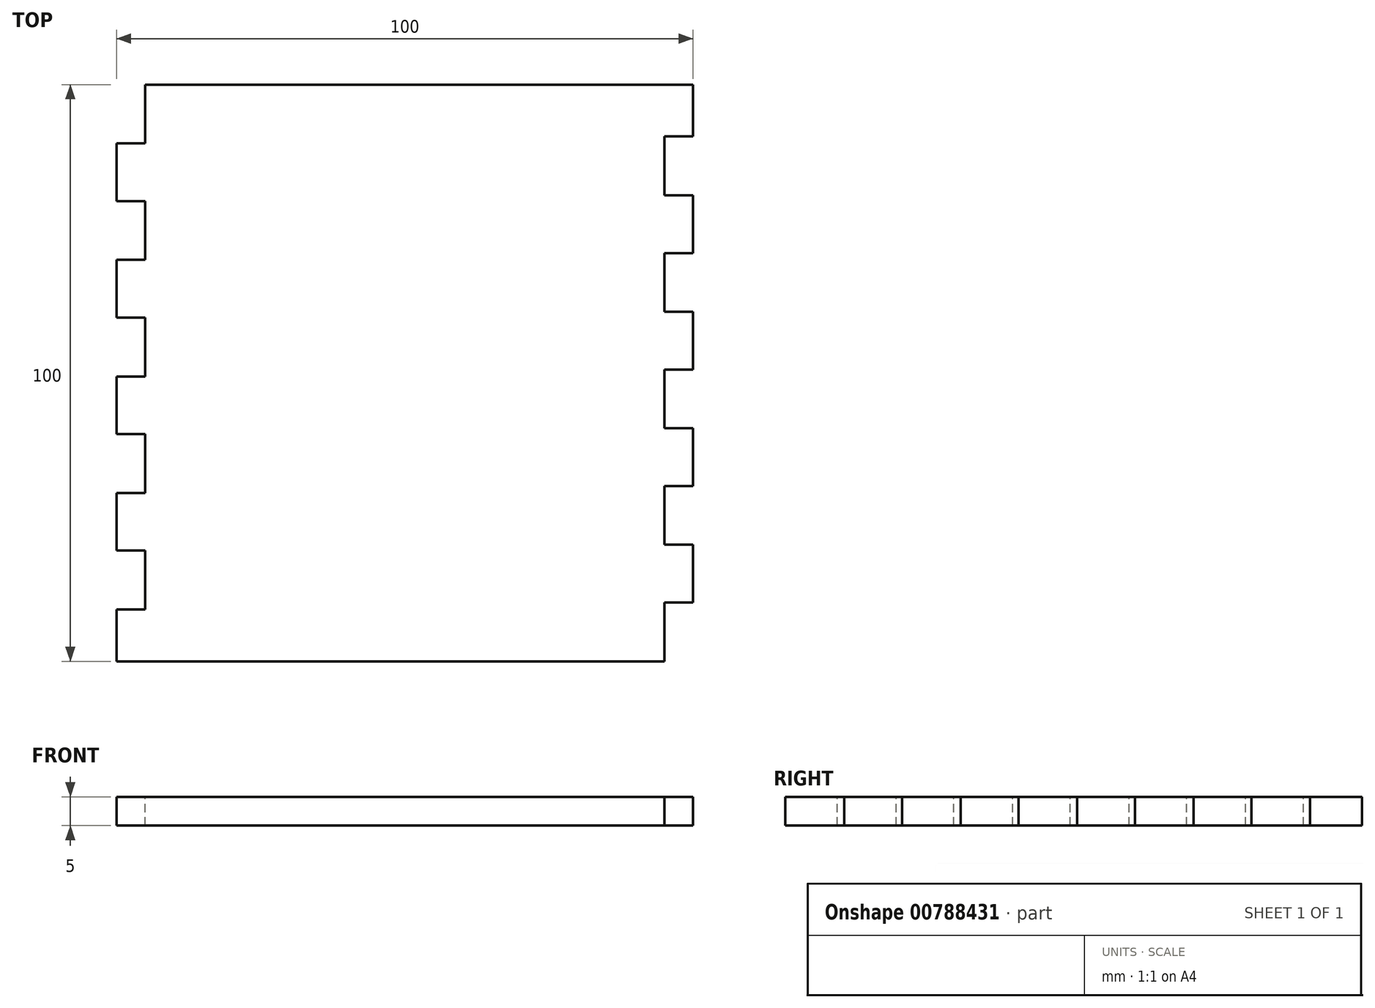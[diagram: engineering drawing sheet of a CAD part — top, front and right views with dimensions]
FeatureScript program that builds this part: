
annotation { "Feature Type Name" : "Feature", "Feature Type Description" : "" }
export const myFeature = defineFeature(function(context is Context, id is Id, definition is map)
    precondition{}
    {
        {
            var Q0;
            Q0=qCreatedBy(makeId("Top.planeOp"),FACE);
            var sketch = newSketch(context, id + "F0", { "sketchPlane" : qUnion([Q0])});
            skLineSegment(sketch, "E0.bottom", {"start": v(50, -50) * mm, "end": v(-50, -50) * mm});
            skLineSegment(sketch, "E0.top", {"start": v(50, 50) * mm, "end": v(-50, 50) * mm});
            skLineSegment(sketch, "E0.left", {"start": v(50, -50) * mm, "end": v(50, 50) * mm});
            skLineSegment(sketch, "E0.right", {"start": v(-50, -50) * mm, "end": v(-50, 50) * mm});
            skPoint(sketch, "E0.middle", {"position": v(0, 0) * mm});
            skSolve(sketch);
        }
        {
            var Q0;
            Q0 = qSketchRegion(id + "F0", true);
            extrude(context, id + "F1", {"entities" : qUnion([Q0]), "depth" : 5 * mm, "offsetDistance" : 25 * mm});
        }
        {
            var Q0;
            Q0=makeQuery(id+"F1.opExtrude","CAP_FACE",FACE,{"disambiguationData":[OSD([sQuery(id+"F0.wireOp",EDGE,"E0.bottom"),sQuery(id+"F0.wireOp",EDGE,"E0.top"),sQuery(id+"F0.wireOp",EDGE,"E0.left"),sQuery(id+"F0.wireOp",EDGE,"E0.right")])],"isStart":false});
            var sketch = newSketch(context, id + "F2", { "sketchPlane" : qUnion([Q0])});
            skLineSegment(sketch, "E1.bottom", {"start": v(-50, 50) * mm, "end": v(-45, 50) * mm});
            skLineSegment(sketch, "E1.top", {"start": v(-50, 39.8) * mm, "end": v(-45, 39.8) * mm});
            skLineSegment(sketch, "E1.left", {"start": v(-50, 50) * mm, "end": v(-50, 39.8) * mm});
            skLineSegment(sketch, "E1.right", {"start": v(-45, 50) * mm, "end": v(-45, 39.8) * mm});
            skLineSegment(sketch, "E2.bottom", {"start": v(-45, 29.8) * mm, "end": v(-50, 29.8) * mm});
            skLineSegment(sketch, "E2.top", {"start": v(-45, 19.6) * mm, "end": v(-50, 19.6) * mm});
            skLineSegment(sketch, "E2.left", {"start": v(-45, 29.8) * mm, "end": v(-45, 19.6) * mm});
            skLineSegment(sketch, "E2.right", {"start": v(-50, 29.8) * mm, "end": v(-50, 19.6) * mm});
            skLineSegment(sketch, "E3.bottom", {"start": v(-45, 9.6) * mm, "end": v(-50, 9.6) * mm});
            skLineSegment(sketch, "E3.top", {"start": v(-45, -0.6) * mm, "end": v(-50, -0.6) * mm});
            skLineSegment(sketch, "E3.left", {"start": v(-45, 9.6) * mm, "end": v(-45, -0.6) * mm});
            skLineSegment(sketch, "E3.right", {"start": v(-50, 9.6) * mm, "end": v(-50, -0.6) * mm});
            skLineSegment(sketch, "E4.bottom", {"start": v(-45, -10.6) * mm, "end": v(-50, -10.6) * mm});
            skLineSegment(sketch, "E4.top", {"start": v(-45, -20.8) * mm, "end": v(-50, -20.8) * mm});
            skLineSegment(sketch, "E4.left", {"start": v(-45, -10.6) * mm, "end": v(-45, -20.8) * mm});
            skLineSegment(sketch, "E4.right", {"start": v(-50, -10.6) * mm, "end": v(-50, -20.8) * mm});
            skLineSegment(sketch, "E5.bottom", {"start": v(-50, -30.8) * mm, "end": v(-45, -30.8) * mm});
            skLineSegment(sketch, "E5.top", {"start": v(-50, -41) * mm, "end": v(-45, -41) * mm});
            skLineSegment(sketch, "E5.left", {"start": v(-50, -30.8) * mm, "end": v(-50, -41) * mm});
            skLineSegment(sketch, "E5.right", {"start": v(-45, -30.8) * mm, "end": v(-45, -41) * mm});
            skSolve(sketch);
        }
        {
            var Q0;
            Q0 = qSketchRegion(id + "F2", true);
            extrude(context, id + "F3", {"entities" : qUnion([Q0]), "operationType" : NewBodyOperationType.REMOVE, "oppositeDirection" : true, "depth" : 5 * mm, "offsetDistance" : 25 * mm});
        }
        {
            var Q0;
            Q0=makeQuery(id+"F1.opExtrude","CAP_FACE",FACE,{"disambiguationData":[OSD([sQuery(id+"F0.wireOp",EDGE,"E0.bottom"),sQuery(id+"F0.wireOp",EDGE,"E0.top"),sQuery(id+"F0.wireOp",EDGE,"E0.left"),sQuery(id+"F0.wireOp",EDGE,"E0.right")])],"isStart":false});
            var sketch = newSketch(context, id + "F4", { "sketchPlane" : qUnion([Q0])});
            skLineSegment(sketch, "E6.bottom", {"start": v(45, -39.8) * mm, "end": v(50, -39.8) * mm});
            skLineSegment(sketch, "E6.top", {"start": v(45, -50) * mm, "end": v(50, -50) * mm});
            skLineSegment(sketch, "E6.left", {"start": v(45, -39.8) * mm, "end": v(45, -50) * mm});
            skLineSegment(sketch, "E6.right", {"start": v(50, -39.8) * mm, "end": v(50, -50) * mm});
            skLineSegment(sketch, "E7.bottom", {"start": v(45, -19.6) * mm, "end": v(50, -19.6) * mm});
            skLineSegment(sketch, "E7.top", {"start": v(45, -29.8) * mm, "end": v(50, -29.8) * mm});
            skLineSegment(sketch, "E7.left", {"start": v(45, -19.6) * mm, "end": v(45, -29.8) * mm});
            skLineSegment(sketch, "E7.right", {"start": v(50, -19.6) * mm, "end": v(50, -29.8) * mm});
            skLineSegment(sketch, "E8.bottom", {"start": v(45, 0.6) * mm, "end": v(50, 0.6) * mm});
            skLineSegment(sketch, "E8.top", {"start": v(45, -9.6) * mm, "end": v(50, -9.6) * mm});
            skLineSegment(sketch, "E8.left", {"start": v(45, 0.6) * mm, "end": v(45, -9.6) * mm});
            skLineSegment(sketch, "E8.right", {"start": v(50, 0.6) * mm, "end": v(50, -9.6) * mm});
            skLineSegment(sketch, "E9.bottom", {"start": v(45, 20.8) * mm, "end": v(50, 20.8) * mm});
            skLineSegment(sketch, "E9.top", {"start": v(45, 10.6) * mm, "end": v(50, 10.6) * mm});
            skLineSegment(sketch, "E9.left", {"start": v(45, 20.8) * mm, "end": v(45, 10.6) * mm});
            skLineSegment(sketch, "E9.right", {"start": v(50, 20.8) * mm, "end": v(50, 10.6) * mm});
            skLineSegment(sketch, "E10.bottom", {"start": v(45, 41) * mm, "end": v(50, 41) * mm});
            skLineSegment(sketch, "E10.top", {"start": v(45, 30.8) * mm, "end": v(50, 30.8) * mm});
            skLineSegment(sketch, "E10.left", {"start": v(45, 41) * mm, "end": v(45, 30.8) * mm});
            skLineSegment(sketch, "E10.right", {"start": v(50, 41) * mm, "end": v(50, 30.8) * mm});
            skSolve(sketch);
        }
        {
            var Q0;
            Q0 = qSketchRegion(id + "F4", true);
            extrude(context, id + "F5", {"entities" : qUnion([Q0]), "operationType" : NewBodyOperationType.REMOVE, "oppositeDirection" : true, "depth" : 5 * mm, "offsetDistance" : 25 * mm});
        }
    });
